AUTODESK INVENTOR PART (.ipt)
format: ipt  version: 2020.3 (Build 243373000, 373)  size: 332,288 bytes
history: native  units: mm
features: extrude x4, sketch x3, plane x1, fillet x1
ambient origin geometry x8: Origin, YZ Plane, XZ Plane, XY Plane, X Axis, Y Axis, Z Axis, Center Point
bodies: Body1 (feature_tree)
feature tree (9):
  sketch  "Sketch1"  dims[d15=8.0mm d16=120.0mm]
  extrude  "Extrusion3"  Depth=120.0mm
  extrude  "Extrusion4"  Depth=98.0mm TaperAngle=0.0deg
  extrude  "Extrusion5"  Depth=10.0mm TaperAngle=0.0deg
  plane  "Work Plane1"
  extrude  "Extrusion6"  Depth=8.0mm TaperAngle=0.0deg
  fillet  "Fillet1"  Radius=4.0mm
  sketch  "Sketch2"  dims[d17=30.0mm d36=98.0mm d37=0.0mm]
  sketch  "Sketch4"  dims[d38=8.0mm d39=0.0mm d45=10.0mm d46=0.0mm d50=8.0mm d51=0.0mm d52=4.0mm d53=4.0mm d54=4.0mm d8=0.5mm d9=0.872665mm d10=0.5mm d11=0.872665mm]
